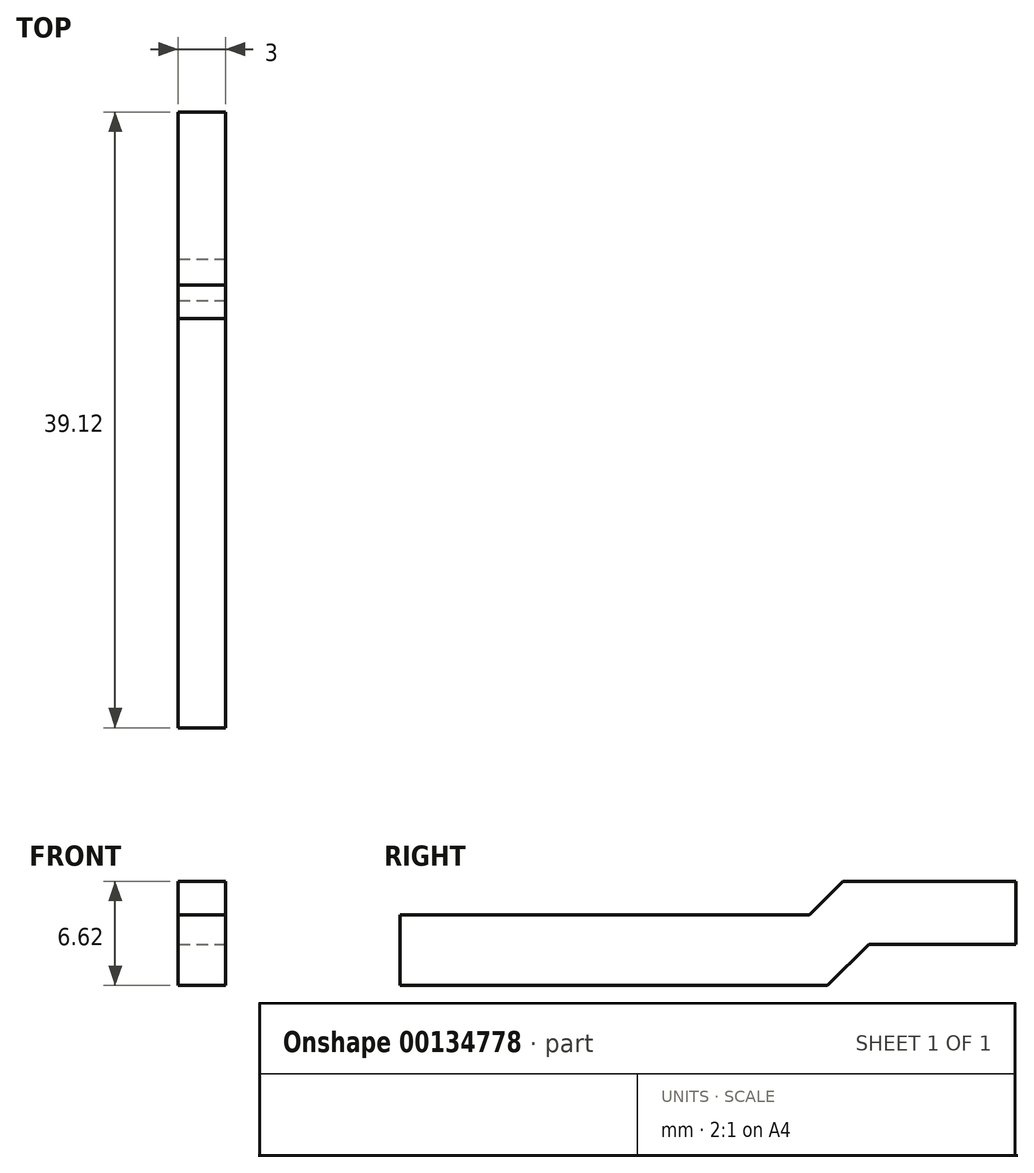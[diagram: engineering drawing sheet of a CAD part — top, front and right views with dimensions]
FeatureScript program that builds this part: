
annotation { "Feature Type Name" : "Feature", "Feature Type Description" : "" }
export const myFeature = defineFeature(function(context is Context, id is Id, definition is map)
    precondition{}
    {
        {
            var Q0;
            Q0=qCreatedBy(makeId("Right.planeOp"),FACE);
            cPlane(context, id + "F0", {"entities" : qUnion([Q0]), "cplaneType" : CPlaneType.OFFSET, "offset" : 11.5 * mm, "oppositeDirection" : true, "width" : 150 * mm, "height" : 150 * mm});
        }
        {
            var Q0;
            Q0=qCreatedBy(id+"F0.planeOp",FACE);
            var sketch = newSketch(context, id + "F1", { "sketchPlane" : qUnion([Q0])});
            skLineSegment(sketch, "E0", {"start": v(0, 0) * mm, "end": v(-11, 0) * mm});
            skLineSegment(sketch, "E1", {"start": v(-11, 0) * mm, "end": v(-13.12, -2.12) * mm});
            skLineSegment(sketch, "E2", {"start": v(-13.12, -2.12) * mm, "end": v(-39.12, -2.12) * mm});
            skLineSegment(sketch, "E3", {"start": v(-39.12, -2.12) * mm, "end": v(-39.12, -6.62) * mm});
            skLineSegment(sketch, "E4", {"start": v(-39.12, -6.62) * mm, "end": v(-11.96, -6.62) * mm});
            skLineSegment(sketch, "E5", {"start": v(-11.96, -6.62) * mm, "end": v(-9.34, -4) * mm});
            skLineSegment(sketch, "E6", {"start": v(-9.34, -4) * mm, "end": v(0, -4) * mm});
            skLineSegment(sketch, "E7", {"start": v(0, -4) * mm, "end": v(0, 0) * mm});
            skSolve(sketch);
        }
        {
            var Q0;
            Q0 = qSketchRegion(id + "F1", true);
            extrude(context, id + "F2", {"entities" : qUnion([Q0]), "oppositeDirection" : true, "depth" : 3 * mm});
        }
    });
